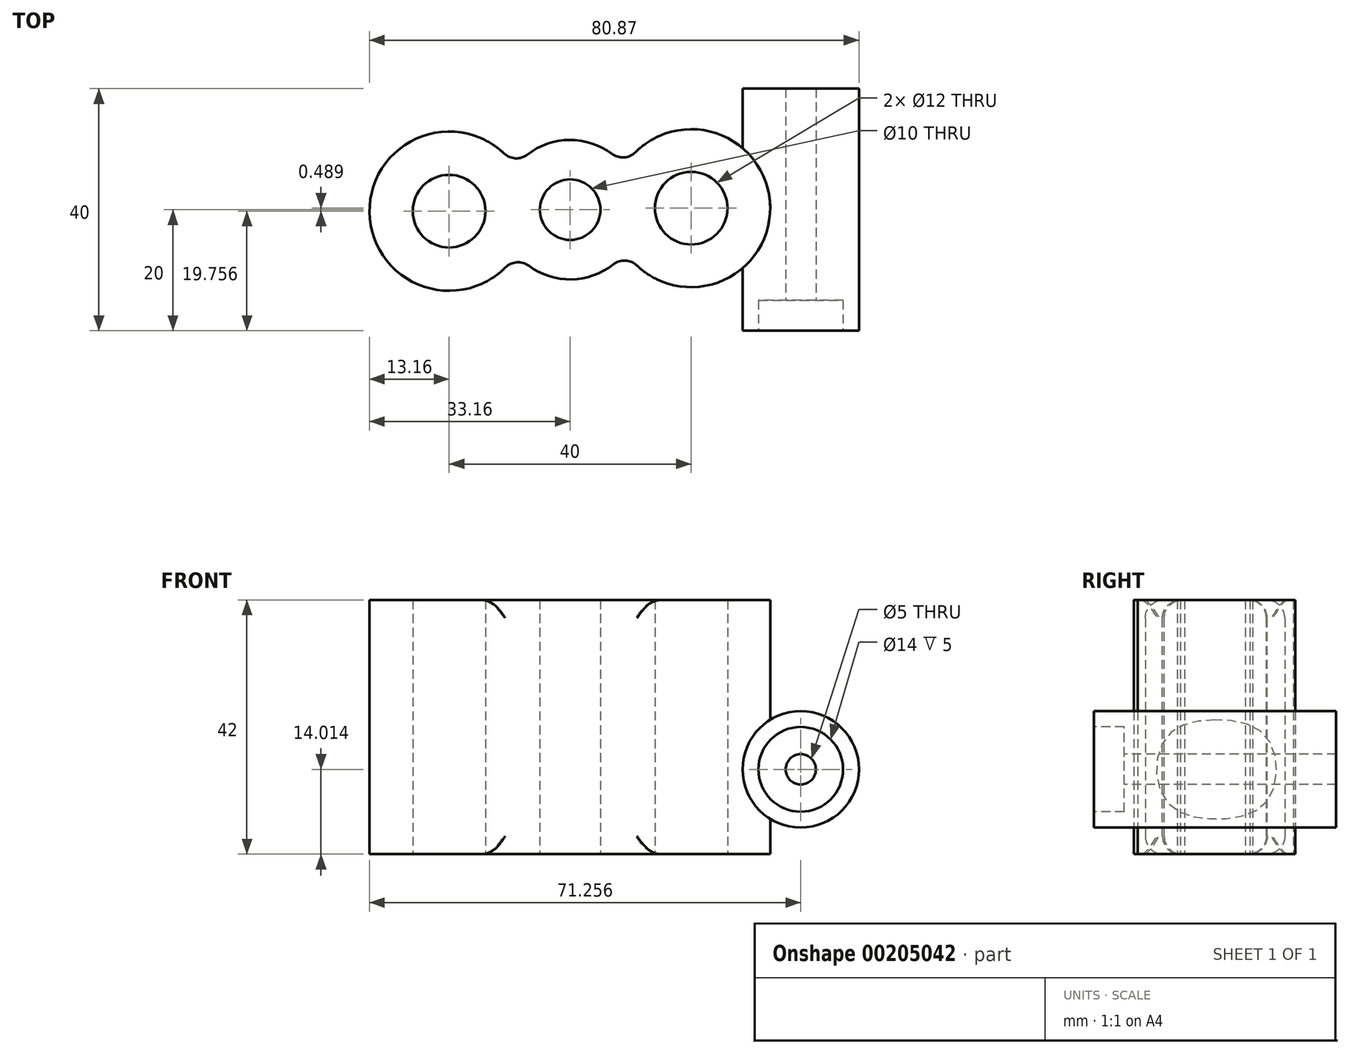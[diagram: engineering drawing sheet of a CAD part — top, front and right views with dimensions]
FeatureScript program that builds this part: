
annotation { "Feature Type Name" : "Feature", "Feature Type Description" : "" }
export const myFeature = defineFeature(function(context is Context, id is Id, definition is map)
    precondition{}
    {
        {
            var Q0;
            Q0=qCreatedBy(makeId("Top.planeOp"),FACE);
            var sketch = newSketch(context, id + "F0", { "sketchPlane" : qUnion([Q0])});
            skCircle(sketch, "E0", {"center": v(20, 0.24) * mm, "radius": 13.05 * mm});
            skCircle(sketch, "E1", {"center": v(0, 0) * mm, "radius": 11.52 * mm});
            skCircle(sketch, "E2", {"center": v(-20, -0.24) * mm, "radius": 13.16 * mm});
            skLineSegment(sketch, "E3", {"start": v(-20, -0.24) * mm, "end": v(20, 0.24) * mm, "construction": true});
            skSolve(sketch);
        }
        {
            var Q0;
            Q0 = qSketchRegion(id + "F0", true);
            var Q1;
            Q1 = qSketchRegion(id + "FJ0h2hpZ6g1TFov_1", true);
            extrude(context, id + "F1", {"entities" : qUnion([Q0, Q1]), "depth" : 42 * mm});
        }
        {
            var Q0;
            Q0=qCreatedBy(makeId("Front.planeOp"),FACE);
            var sketch = newSketch(context, id + "F2", { "sketchPlane" : qUnion([Q0])});
            skCircle(sketch, "E4", {"center": v(38.1, 14.01) * mm, "radius": 9.62 * mm});
            skPoint(sketch, "E5.start.orphan", {"position": v(33.04, 0) * mm});
            skSolve(sketch);
        }
        {
            var Q0;
            Q0 = qSketchRegion(id + "F2", true);
            extrude(context, id + "F3", {"entities" : qUnion([Q0]), "operationType" : NewBodyOperationType.ADD, "depth" : 20 * mm});
        }
        {
            var Q0;
            Q0 = qSketchRegion(id + "F2", true);
            extrude(context, id + "F4", {"entities" : qUnion([Q0]), "operationType" : NewBodyOperationType.ADD, "oppositeDirection" : true, "depth" : 20 * mm});
        }
        {
            var Q0;
            Q0=sQuery(id+"F0.wireOp",VERTEX,"E3.start");
            var Q1;
            Q1=sQuery(id+"F0.wireOp",VERTEX,"E0.center");
            var Q2;
            Q2=makeQuery(id+"F1.opExtrude","SWEPT_BODY",BODY,{"disambiguationData":[OSD([sQuery(id+"F0.wireOp",EDGE,"E0"),sQuery(id+"F0.wireOp",EDGE,"E1"),sQuery(id+"F0.wireOp",EDGE,"E2")])]});
            hole(context, id + "F5", {"style" : HoleStyle.SIMPLE, "endStyle" : HoleEndStyle.THROUGH, "oppositeDirection" : true, "holeDiameter" : 12 * mm, "locations" : qUnion([Q0, Q1]), "scope" : qUnion([Q2]), "isTappedThrough" : true});
        }
        {
            var Q0;
            Q0=sQuery(id+"F0.wireOp",VERTEX,"E1.center");
            var Q1;
            Q1=makeQuery(id+"F1.opExtrude","SWEPT_BODY",BODY,{"disambiguationData":[OSD([sQuery(id+"F0.wireOp",EDGE,"E0"),sQuery(id+"F0.wireOp",EDGE,"E1"),sQuery(id+"F0.wireOp",EDGE,"E2")])]});
            hole(context, id + "F6", {"style" : HoleStyle.SIMPLE, "endStyle" : HoleEndStyle.THROUGH, "oppositeDirection" : true, "holeDiameter" : 10 * mm, "locations" : qUnion([Q0]), "scope" : qUnion([Q1]), "isTappedThrough" : true});
        }
        {
            var Q0;
            Q0=makeQuery(id+"F3.opExtrude","CAP_FACE",FACE,{"disambiguationData":[OSD([sQuery(id+"F2.wireOp",EDGE,"E4")])],"isStart":false});
            var sketch = newSketch(context, id + "F7", { "sketchPlane" : qUnion([Q0])});
            skCircle(sketch, "E6", {"center": v(38.1, 14.01) * mm, "radius": 9.63 * mm});
            skSolve(sketch);
        }
        {
            var Q0;
            Q0=sQuery(id+"F7.wireOp",VERTEX,"E6.center");
            var Q1;
            Q1=makeQuery(id+"F1.opExtrude","SWEPT_BODY",BODY,{"disambiguationData":[OSD([sQuery(id+"F0.wireOp",EDGE,"E0"),sQuery(id+"F0.wireOp",EDGE,"E1"),sQuery(id+"F0.wireOp",EDGE,"E2")])]});
            hole(context, id + "F8", {"style" : HoleStyle.C_BORE, "endStyle" : HoleEndStyle.THROUGH, "holeDiameter" : 5 * mm, "cBoreDiameter" : 14 * mm, "cBoreDepth" : 5 * mm, "locations" : qUnion([Q0]), "scope" : qUnion([Q1]), "isTappedThrough" : true});
        }
        {
            var Q0;
            {var subQ0=sQuery(id+"F0.wireOp",EDGE,"E1");Q0=makeQuery(id+"F1.opExtrude","SWEPT_FACE",FACE,{"disambiguationData":[OSD([subQ0]),TDD([makeQuery(id+"F0.imprint","IMPRINT",EDGE,{"disambiguationData":[TD([[makeQuery(id+"F0.imprint","INTERSECT",VERTEX,{"disambiguationData":[OD(1.0)],"derivedFrom":[sQuery(id+"F0.wireOp",EDGE,"E0"),subQ0]}),1.0]])],"derivedFrom":subQ0})])]});}
            var Q1;
            {var subQ0=sQuery(id+"F0.wireOp",EDGE,"E1");Q1=makeQuery(id+"F1.opExtrude","SWEPT_FACE",FACE,{"disambiguationData":[OSD([subQ0]),TDD([makeQuery(id+"F0.imprint","IMPRINT",EDGE,{"disambiguationData":[TD([[makeQuery(id+"F0.imprint","INTERSECT",VERTEX,{"disambiguationData":[OD(0.0)],"derivedFrom":[sQuery(id+"F0.wireOp",EDGE,"E0"),subQ0]}),-1.0]])],"derivedFrom":subQ0})])]});}
            fillet(context, id + "F9", {"entities" : qUnion([Q0, Q1]), "radius" : 3 * mm, "tangentPropagation" : true, "allowEdgeOverflow" : false});
        }
    });
